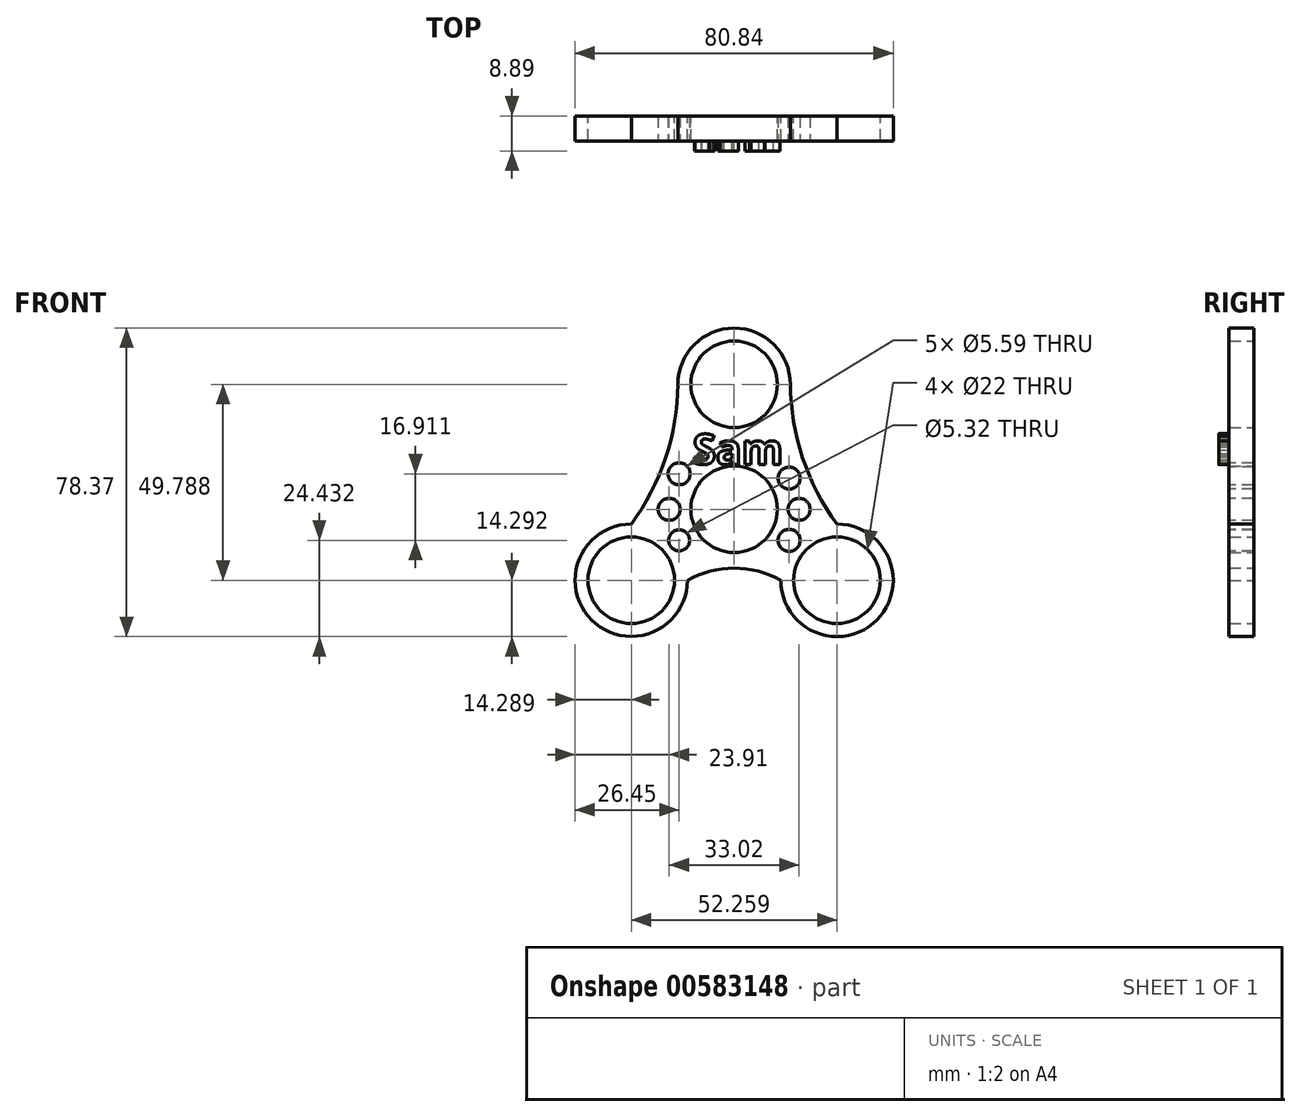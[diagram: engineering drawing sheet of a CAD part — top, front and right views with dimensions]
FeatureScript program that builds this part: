
annotation { "Feature Type Name" : "Feature", "Feature Type Description" : "" }
export const myFeature = defineFeature(function(context is Context, id is Id, definition is map)
    precondition{}
    {
        {
            var Q0;
            Q0=qCreatedBy(makeId("Front.planeOp"),FACE);
            var sketch = newSketch(context, id + "F0", { "sketchPlane" : qUnion([Q0])});
            skCircle(sketch, "E0", {"center": v(0, 0) * mm, "radius": 14.29 * mm});
            skCircle(sketch, "E1", {"center": v(0, 31.75) * mm, "radius": 14.29 * mm});
            skCircle(sketch, "E2", {"center": v(0, 31.75) * mm, "radius": 11 * mm});
            skCircle(sketch, "E3", {"center": v(0, 0) * mm, "radius": 11 * mm});
            skCircle(sketch, "E4", {"center": v(-26.13, -18.03) * mm, "radius": 11 * mm});
            skCircle(sketch, "E5", {"center": v(-26.13, -18.03) * mm, "radius": 14.29 * mm});
            skCircle(sketch, "E6", {"center": v(26.13, -18.04) * mm, "radius": 11 * mm});
            skCircle(sketch, "E7", {"center": v(26.13, -18.04) * mm, "radius": 14.29 * mm});
            skArc(sketch, "E8", {"start": v(11.84, -18.04) * mm, "mid": v(0, -14.97) * mm, "end": v(-11.84, -18.03) * mm});
            skArc(sketch, "E9", {"start": v(14.29, 31.75) * mm, "mid": v(17.41, 13.07) * mm, "end": v(26.13, -3.75) * mm});
            skArc(sketch, "E10", {"start": v(-26.13, -3.75) * mm, "mid": v(-17.42, 13.07) * mm, "end": v(-14.29, 31.75) * mm});
            skSolve(sketch);
        }
        {
            var Q0;
            Q0=makeQuery(id+"F0.imprint","IMPRINT",FACE,{"disambiguationData":[TD([[makeQuery(id+"F0.imprint","IMPRINT",EDGE,{"derivedFrom":sQuery(id+"F0.wireOp",EDGE,"E0")}),-1.0]])]});
            var Q1;
            Q1=makeQuery(id+"F0.imprint","IMPRINT",FACE,{"disambiguationData":[TD([[makeQuery(id+"F0.imprint","IMPRINT",EDGE,{"derivedFrom":sQuery(id+"F0.wireOp",EDGE,"E2")}),-1.0]])]});
            var Q2;
            Q2=makeQuery(id+"F0.imprint","IMPRINT",FACE,{"disambiguationData":[TD([[makeQuery(id+"F0.imprint","IMPRINT",EDGE,{"derivedFrom":sQuery(id+"F0.wireOp",EDGE,"E6")}),-1.0]])]});
            var Q3;
            Q3=makeQuery(id+"F0.imprint","IMPRINT",FACE,{"disambiguationData":[TD([[makeQuery(id+"F0.imprint","IMPRINT",EDGE,{"derivedFrom":sQuery(id+"F0.wireOp",EDGE,"E0")}),1.0]])]});
            var Q4;
            Q4=makeQuery(id+"F0.imprint","IMPRINT",FACE,{"disambiguationData":[TD([[makeQuery(id+"F0.imprint","IMPRINT",EDGE,{"derivedFrom":sQuery(id+"F0.wireOp",EDGE,"E4")}),-1.0]])]});
            extrude(context, id + "F1", {"entities" : qUnion([Q0, Q1, Q2, Q3, Q4]), "depth" : 6.35 * mm, "offsetDistance" : 25.4 * mm});
        }
        {
            var Q0;
            Q0=makeQuery(id+"F1.opExtrude","CAP_FACE",FACE,{"disambiguationData":[OSD([sQuery(id+"F0.wireOp",EDGE,"E1"),sQuery(id+"F0.wireOp",EDGE,"E2"),sQuery(id+"F0.wireOp",EDGE,"E3"),sQuery(id+"F0.wireOp",EDGE,"E4"),sQuery(id+"F0.wireOp",EDGE,"E5"),sQuery(id+"F0.wireOp",EDGE,"E6"),sQuery(id+"F0.wireOp",EDGE,"E7"),sQuery(id+"F0.wireOp",EDGE,"E8"),sQuery(id+"F0.wireOp",EDGE,"E9"),sQuery(id+"F0.wireOp",EDGE,"E10")])],"isStart":false});
            var sketch = newSketch(context, id + "F2", { "sketchPlane" : qUnion([Q0])});
            skText(sketch, "E11", { "text": "Sam", "fontName": "OpenSans-Bold.ttf"});
            const initialGuessF2  = {"E11": [-0.01052, 0.01143, 1, 0, 0.00772]};
            skSetInitialGuess(sketch, initialGuessF2);
            skSolve(sketch);
        }
        {
            var Q0;
            Q0 = qSketchRegion(id + "F2", true);
            extrude(context, id + "F3", {"entities" : qUnion([Q0]), "operationType" : NewBodyOperationType.ADD, "depth" : 2.54 * mm, "offsetDistance" : 25.4 * mm});
        }
        {
            var Q0;
            {var subQ0=sQuery(id+"F0.wireOp",EDGE,"E9");var subQ1=sQuery(id+"F0.wireOp",EDGE,"E8");var subQ2=sQuery(id+"F0.wireOp",EDGE,"E7");var subQ3=sQuery(id+"F0.wireOp",EDGE,"E6");var subQ4=sQuery(id+"F0.wireOp",EDGE,"E5");var subQ5=sQuery(id+"F0.wireOp",EDGE,"E10");var subQ6=sQuery(id+"F0.wireOp",EDGE,"E1");var subQ7=sQuery(id+"F0.wireOp",EDGE,"E4");var subQ8=sQuery(id+"F0.wireOp",EDGE,"E2");var subQ9=sQuery(id+"F0.wireOp",EDGE,"E3");Q0=makeQuery(id+"F3.boolean.opBoolean","SPLIT",FACE,{"disambiguationData":[TD([makeQuery(id+"F1.opExtrude","SWEPT_FACE",FACE,{"disambiguationData":[OSD([subQ6])]})])],"derivedFrom":makeQuery(id+"F1.opExtrude","CAP_FACE",FACE,{"disambiguationData":[OSD([subQ6,subQ8,subQ9,subQ7,subQ4,subQ3,subQ2,subQ1,subQ0,subQ5])],"isStart":false})});}
            var sketch = newSketch(context, id + "F4", { "sketchPlane" : qUnion([Q0])});
            skCircle(sketch, "E12", {"center": v(-16.51, 0) * mm, "radius": 2.8 * mm});
            skCircle(sketch, "E13", {"center": v(16.51, 0) * mm, "radius": 2.8 * mm});
            skCircle(sketch, "E14", {"center": v(-13.97, 9.01) * mm, "radius": 2.8 * mm});
            skCircle(sketch, "E15", {"center": v(13.97, 7.92) * mm, "radius": 2.8 * mm});
            skCircle(sketch, "E16", {"center": v(-13.97, -7.9) * mm, "radius": 2.66 * mm});
            skCircle(sketch, "E17", {"center": v(13.97, -7.9) * mm, "radius": 2.8 * mm});
            skSolve(sketch);
        }
        {
            var Q0;
            Q0=makeQuery(id+"F4.imprint","IMPRINT",FACE,{"disambiguationData":[TD([[makeQuery(id+"F4.imprint","IMPRINT",EDGE,{"derivedFrom":sQuery(id+"F4.wireOp",EDGE,"E14")}),1.0]])]});
            var Q1;
            Q1=makeQuery(id+"F4.imprint","IMPRINT",FACE,{"disambiguationData":[TD([[makeQuery(id+"F4.imprint","IMPRINT",EDGE,{"derivedFrom":sQuery(id+"F4.wireOp",EDGE,"E12")}),1.0]])]});
            var Q2;
            Q2=makeQuery(id+"F4.imprint","IMPRINT",FACE,{"disambiguationData":[TD([[makeQuery(id+"F4.imprint","IMPRINT",EDGE,{"derivedFrom":sQuery(id+"F4.wireOp",EDGE,"E16")}),1.0]])]});
            var Q3;
            Q3=makeQuery(id+"F4.imprint","IMPRINT",FACE,{"disambiguationData":[TD([[makeQuery(id+"F4.imprint","IMPRINT",EDGE,{"derivedFrom":sQuery(id+"F4.wireOp",EDGE,"E17")}),1.0]])]});
            var Q4;
            Q4=makeQuery(id+"F4.imprint","IMPRINT",FACE,{"disambiguationData":[TD([[makeQuery(id+"F4.imprint","IMPRINT",EDGE,{"derivedFrom":sQuery(id+"F4.wireOp",EDGE,"E13")}),1.0]])]});
            var Q5;
            Q5=makeQuery(id+"F4.imprint","IMPRINT",FACE,{"disambiguationData":[TD([[makeQuery(id+"F4.imprint","IMPRINT",EDGE,{"derivedFrom":sQuery(id+"F4.wireOp",EDGE,"E15")}),1.0]])]});
            extrude(context, id + "F5", {"entities" : qUnion([Q0, Q1, Q2, Q3, Q4, Q5]), "operationType" : NewBodyOperationType.REMOVE, "oppositeDirection" : true, "depth" : 25.4 * mm, "offsetDistance" : 25.4 * mm});
        }
    });
